# Revit family: Indirect-Water-Heater_Lochinvar_Ltd-SIVS-110_G_E
name_source: partatom
category: Mechanical Equipment
revit_build: Autodesk Revit Architecture 2013 (Build: 20130531_2115(x64)
units: mm (PartAtom-declared; Revit-internal decimal feet)

## types (1)
- Indirect-Water-Heater_Lochinvar_Ltd-SIVS-110_G_E
    1e Maintenance (check-up) = 3 months after installation
    2nd Maintenance (general maintenance) = 12 months after installation
    Assembly Code = D3010
    BIM Content Developer = CAD & Comapny
    BIM Content Developer URL = http://www.cadcompany.nl
    Cold Water Connection R = 2"
    Description = Indirect Water Heater
    Destination / Counrty = UK & Ireland
    Diameter (with insulation) = 360 mm  [stored 1.1811 ft]
    Diameter (without insulation) = 303 mm  [stored 0.994094 ft]
    Draw-off Capacity @ ΔT = 28°C after 120 min. = 6935.0 L
    Draw-off Capacity @ ΔT = 28°C after 30 min. = 2328.0 L
    Draw-off Capacity @ ΔT = 28°C after 60 min. = 3864.0 L
    Draw-off Capacity @ ΔT = 28°C after 90 min. = 5400.0 L
    Draw-off Capacity @ ΔT = 44°C after 120 min. = 4413.0 L
    Draw-off Capacity @ ΔT = 44°C after 30 min. = 1482.0 L
    Draw-off Capacity @ ΔT = 44°C after 60 min. = 2459.0 L
    Draw-off Capacity @ ΔT = 44°C after 90 min. = 3436.0 L
    Draw-off Capacity @ ΔT = 50°C after 120 min. = 3884.0 L
    Draw-off Capacity @ ΔT = 50°C after 30 min. = 1304.0 L
    Draw-off Capacity @ ΔT = 50°C after 60 min. = 2164.0 L
    Draw-off Capacity @ ΔT = 50°C after 90 min. = 3024.0 L
    Draw-off Capacity @ ΔT = 55°C after 120 min. = 3531.0 L
    Draw-off Capacity @ ΔT = 55°C after 30 min. = 1185.0 L
    Draw-off Capacity @ ΔT = 55°C after 60 min. = 1967.0 L
    Draw-off Capacity @ ΔT = 55°C after 90 min. = 2749.0 L
    Draw-off Capacity @ ΔT = 70°C after 120 min. = 2774.0 L
    Draw-off Capacity @ ΔT = 70°C after 30 min. = 931.0 L
    Draw-off Capacity @ ΔT = 70°C after 60 min. = 1546.0 L
    Draw-off Capacity @ ΔT = 70°C after 90 min. = 2160.0 L
    Empty Weight = 180.00 kg
    Flow Rate - Volume L/h = 4300
    Heating Up Time @ ΔT = 28°C = 9
    Heating Up Time @ ΔT = 44°C = 15
    Heating Up Time @ ΔT = 50°C = 16
    Heating Up Time @ ΔT = 55°C = 18
    Heating Up Time @ ΔT = 70°C = 23
    Height (with insulation) = 2070 mm  [stored 6.79134 ft]
    Height (without insulation) = 2013 mm
    Height Cold Water Inlet = 70 mm  [stored 0.229659 ft]
    Height Warm Water Outlet = 2010 mm  [stored 6.59449 ft]
    Hot / Warm Water Connection R = 2"
    Insulation Thickness = 57 mm  [stored 0.187008 ft]
    Length = 0 mm  [stored 0 ft]
    Maintenance Interval = 12 months
    Manufacturer = Lochinvar Limited
    Manufacturer Number = E 7110
E 7110
E 7110
    Max. Operating Pressure - heat exchanger = 1600000.0 Pa
    Max. Operating Pressure - tank = 1000000.0 Pa
    Max. Temperature - heat exchanger = 110 °C
    Max. Temperature - tank = 95 °C
    Model = SIVS 110 G E
    Nominal Output - heat exchanger = 102000 W
    Operating Weight = 660.00 kg
    Packaging Height = 2150 mm
    Packaging Length = 780 mm  [stored 2.55906 ft]
    Packaging Width = 780 mm  [stored 2.55906 ft]
    Pressure Loss - heat exchanger 80ºC/60ºC = 48900.0 Pa
    Product Documentation Link = http://www.lochinvar.ltd.uk
    Product Instruction Link = http://www.lochinvar.ltd.uk
    Recovery Rate @ ΔT = 28°C (ltr/hr) = 3071
    Recovery Rate @ ΔT = 44°C (ltr/hr) = 1955
    Recovery Rate @ ΔT = 50°C (ltr/hr) = 1720
    Recovery Rate @ ΔT = 55°C (ltr/hr) = 1564
    Recovery Rate @ ΔT = 70°C (ltr/hr) = 1229
    Serial Number = 8717449269203
    Stand-by Loss = 0 W
    Stand-by Loss - daily (Watt/24H) = 0
    Storage Capacity - heat exchanger = 18.8 m³
    Storage Capacity - tank = 480 m³
    Surface Heat Exchanger = 3.11 m²
    T&P Connection Rp = 1"
    Transport Weight = 201.00 kg
    Type of Packaging = Plastic and Wood
    URL = www.lochinvar.ltd.uk
    Warranty on Parts = 12 months
    Warranty on Tank = 36 months
    Width = 0 mm  [stored 0 ft]
    Workspace = 820 mm  [stored 2.69029 ft]

note: [stored X ft] marks values corroborated as IEEE doubles in the binary element streams (Revit-internal decimal feet)

## geometry (parser evidence)
native form markers: Sweep x14
no freeform markers — native parametric forms only
